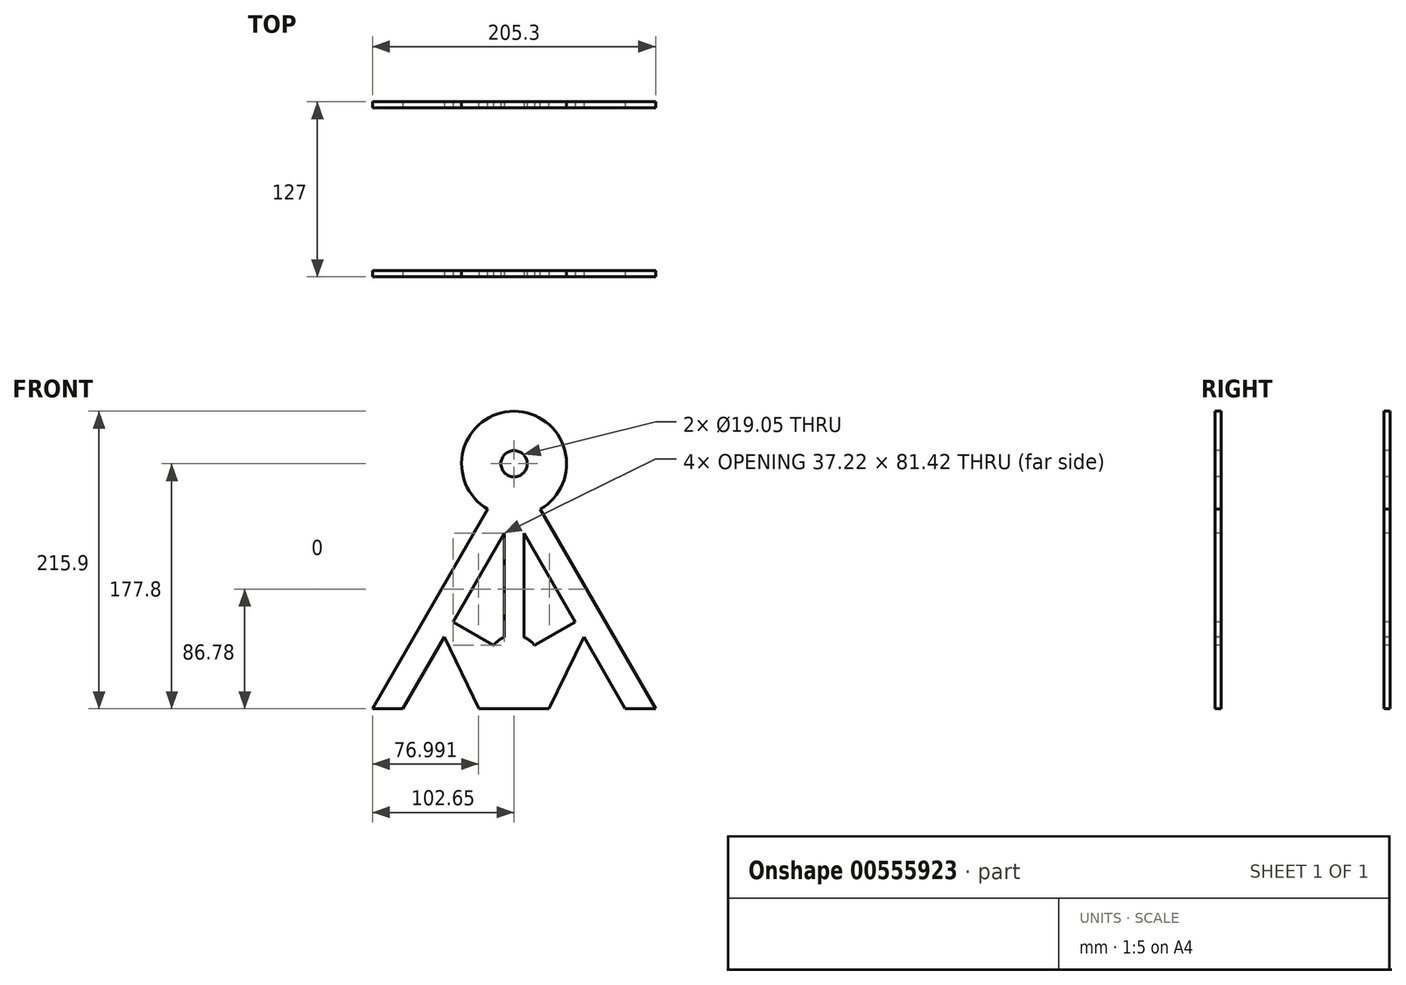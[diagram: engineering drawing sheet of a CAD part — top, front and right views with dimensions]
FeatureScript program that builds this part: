
annotation { "Feature Type Name" : "Feature", "Feature Type Description" : "" }
export const myFeature = defineFeature(function(context is Context, id is Id, definition is map)
    precondition{}
    {
        {
            var Q0;
            Q0=qCreatedBy(makeId("Front.planeOp"),FACE);
            var sketch = newSketch(context, id + "F0", { "sketchPlane" : qUnion([Q0])});
            skArc(sketch, "E0", {"start": v(-228.6, 0) * mm, "mid": v(0, -228.6) * mm, "end": v(228.6, 0) * mm});
            skLineSegment(sketch, "E1", {"start": v(-38.1, 0) * mm, "end": v(-228.6, 0) * mm});
            skLineSegment(sketch, "E2", {"start": v(38.1, 0) * mm, "end": v(228.6, 0) * mm});
            skLineSegment(sketch, "E3", {"start": v(-19.05, -33) * mm, "end": v(-114.3, -197.97) * mm});
            skLineSegment(sketch, "E4", {"start": v(19.05, -33) * mm, "end": v(114.3, -197.97) * mm});
            skArc(sketch, "E5", {"start": v(19.05, -33) * mm, "mid": v(0, 38.1) * mm, "end": v(-19.05, -33) * mm});
            skSolve(sketch);
        }
        {
            var Q0;
            {var subQ3=sQuery(id+"F0.wireOp",EDGE,"E3");Q0=makeQuery(id+"F0.imprint","IMPRINT",FACE,{"disambiguationData":[TD([[makeQuery(id+"F0.imprint","IMPRINT",EDGE,{"derivedFrom":subQ3}),1.0]])]});}
            extrude(context, id + "F1", {"entities" : qUnion([Q0]), "depth" : 127 * mm, "offsetDistance" : 25.4 * mm});
        }
        {
            var Q0;
            Q0=makeQuery(id+"F1.opExtrude","SWEPT_FACE",FACE,{"disambiguationData":[OSD([sQuery(id+"F0.wireOp",EDGE,"E5")])]});
            var Q1;
            Q1=makeQuery(id+"F1.opExtrude","SWEPT_FACE",FACE,{"disambiguationData":[OSD([sQuery(id+"F0.wireOp",EDGE,"E4")])]});
            var Q2;
            Q2=makeQuery(id+"F1.opExtrude","SWEPT_FACE",FACE,{"disambiguationData":[OSD([sQuery(id+"F0.wireOp",EDGE,"E3")])]});
            shell(context, id + "F2", {"entities" : qUnion([Q0, Q1, Q2]), "thickness" : 4.44 * mm});
        }
        {
            var Q0;
            Q0=makeQuery(id+"F1.opExtrude","CAP_FACE",FACE,{"disambiguationData":[OSD([sQuery(id+"F0.wireOp",EDGE,"E0"),sQuery(id+"F0.wireOp",EDGE,"E3"),sQuery(id+"F0.wireOp",EDGE,"E4"),sQuery(id+"F0.wireOp",EDGE,"E5")])],"isStart":false});
            var sketch = newSketch(context, id + "F3", { "sketchPlane" : qUnion([Q0])});
            skLineSegment(sketch, "E6.0", {"start": v(7.05, -50.3) * mm, "end": v(87.84, -190.25) * mm});
            skArc(sketch, "E6.1", {"start": v(-87.84, -190.25) * mm, "mid": v(-48.4, -203.88) * mm, "end": v(-7.05, -209.43) * mm});
            skCircle(sketch, "E7", {"center": v(0, 0) * mm, "radius": 9.53 * mm});
            skLineSegment(sketch, "E8", {"start": v(-7.05, -50.3) * mm, "end": v(-7.05, -125.9) * mm});
            skLineSegment(sketch, "E9", {"start": v(7.05, -50.3) * mm, "end": v(7.05, -125.9) * mm});
            skLineSegment(sketch, "E10", {"start": v(-87.84, -190.25) * mm, "end": v(-50.62, -125.78) * mm});
            skPoint(sketch, "E11.endSnap0", {"position": v(-66.67, -115.48) * mm});
            skLineSegment(sketch, "E12", {"start": v(-44.27, -114.78) * mm, "end": v(-14.9, -131.73) * mm});
            skLineSegment(sketch, "E13.trimOffspring", {"start": v(-7.05, -169.35) * mm, "end": v(-7.05, -209.43) * mm});
            skLineSegment(sketch, "E14.trimOffspring", {"start": v(-50.62, -125.78) * mm, "end": v(-87.84, -190.25) * mm});
            skArc(sketch, "E15.trimOffspring", {"start": v(7.05, -209.43) * mm, "mid": v(48.4, -203.88) * mm, "end": v(87.84, -190.25) * mm});
            skLineSegment(sketch, "E16", {"start": v(-7.05, -50.3) * mm, "end": v(0, -50.3) * mm, "construction": true});
            skLineSegment(sketch, "E17", {"start": v(0, -50.3) * mm, "end": v(0, -85.39) * mm, "construction": true});
            skLineSegment(sketch, "E18", {"start": v(-44.27, -114.78) * mm, "end": v(-7.05, -50.3) * mm});
            skLineSegment(sketch, "E19.MirrorCS", {"start": v(44.27, -114.78) * mm, "end": v(14.9, -131.73) * mm});
            skLineSegment(sketch, "E20.trimOffspring", {"start": v(7.05, -169.35) * mm, "end": v(7.05, -209.43) * mm});
            skArc(sketch, "E21", {"start": v(14.9, -131.73) * mm, "mid": v(11.36, -128.3) * mm, "end": v(7.05, -125.9) * mm});
            skPoint(sketch, "E22.orphan", {"position": v(7.05, -136.27) * mm});
            skPoint(sketch, "E23.orphan", {"position": v(7.05, -150.93) * mm});
            skPoint(sketch, "E24.orphan", {"position": v(-7.05, -150.93) * mm});
            skPoint(sketch, "E25.orphan", {"position": v(-7.05, -136.27) * mm});
            skLineSegment(sketch, "E26", {"start": v(50.62, -125.78) * mm, "end": v(7.05, -169.35) * mm, "construction": true});
            skLineSegment(sketch, "E27", {"start": v(50.62, -125.78) * mm, "end": v(7.05, -169.35) * mm});
            skLineSegment(sketch, "E28.MirrorCS", {"start": v(-50.62, -125.78) * mm, "end": v(-7.05, -169.35) * mm});
            skArc(sketch, "E29.trimOffspring", {"start": v(-7.05, -125.9) * mm, "mid": v(-11.36, -128.3) * mm, "end": v(-14.9, -131.73) * mm});
            skSolve(sketch);
        }
        {
            var Q0;
            Q0=makeQuery(id+"F3.imprint","IMPRINT",FACE,{"disambiguationData":[TD([[makeQuery(id+"F3.imprint","IMPRINT",EDGE,{"derivedFrom":sQuery(id+"F3.wireOp",EDGE,"E6.1")}),1.0]])]});
            var Q1;
            {var subQ2=sQuery(id+"F3.wireOp",EDGE,"E15.trimOffspring");Q1=makeQuery(id+"F3.imprint","IMPRINT",FACE,{"disambiguationData":[TD([[makeQuery(id+"F3.imprint","IMPRINT",EDGE,{"derivedFrom":subQ2}),1.0]])]});}
            var Q2;
            {var subQ0=sQuery(id+"F3.wireOp",EDGE,"E9");Q2=makeQuery(id+"F3.imprint","IMPRINT",FACE,{"disambiguationData":[TD([[makeQuery(id+"F3.imprint","IMPRINT",EDGE,{"derivedFrom":subQ0}),1.0]])]});}
            var Q3;
            {var subQ0=sQuery(id+"F3.wireOp",EDGE,"E8");Q3=makeQuery(id+"F3.imprint","IMPRINT",FACE,{"disambiguationData":[TD([[makeQuery(id+"F3.imprint","IMPRINT",EDGE,{"derivedFrom":subQ0}),-1.0]])]});}
            var Q4;
            Q4=makeQuery(id+"F3.imprint","IMPRINT",FACE,{"disambiguationData":[TD([[makeQuery(id+"F3.imprint","IMPRINT",EDGE,{"derivedFrom":sQuery(id+"F3.wireOp",EDGE,"E7")}),1.0]])]});
            var Q5;
            Q5=makeQuery(id+"F1.opExtrude","CAP_FACE",FACE,{"disambiguationData":[OSD([sQuery(id+"F0.wireOp",EDGE,"E0"),sQuery(id+"F0.wireOp",EDGE,"E3"),sQuery(id+"F0.wireOp",EDGE,"E4"),sQuery(id+"F0.wireOp",EDGE,"E5")])],"isStart":true});
            extrude(context, id + "F4", {"entities" : qUnion([Q0, Q1, Q2, Q3, Q4]), "operationType" : NewBodyOperationType.REMOVE, "endBound" : BoundingType.UP_TO_SURFACE, "oppositeDirection" : true, "depth" : 25.4 * mm, "endBoundEntityFace" : qUnion([Q5]), "offsetDistance" : 25.4 * mm});
        }
        {
            var Q0;
            Q0=qCreatedBy(makeId("Front.planeOp"),FACE);
            var sketch = newSketch(context, id + "F5", { "sketchPlane" : qUnion([Q0])});
            skLineSegment(sketch, "E30", {"start": v(0, -228.6) * mm, "end": v(114.3, -228.6) * mm});
            skLineSegment(sketch, "E31", {"start": v(0, -228.6) * mm, "end": v(-114.3, -228.6) * mm});
            skLineSegment(sketch, "E32", {"start": v(114.3, -197.97) * mm, "end": v(114.3, -228.6) * mm});
            skLineSegment(sketch, "E33", {"start": v(-114.3, -197.97) * mm, "end": v(-114.3, -228.6) * mm});
            skPoint(sketch, "E34.orphan", {"position": v(-122.47, -228.6) * mm});
            skArc(sketch, "E35.0", {"start": v(-114.3, -197.97) * mm, "mid": v(0, -228.6) * mm, "end": v(114.3, -197.97) * mm});
            skLineSegment(sketch, "E36", {"start": v(114.3, -228.6) * mm, "end": v(107.95, -228.6) * mm, "construction": true});
            skLineSegment(sketch, "E37", {"start": v(107.95, -228.6) * mm, "end": v(107.95, -222.25) * mm, "construction": true});
            skLineSegment(sketch, "E38.bottom", {"start": v(107.95, -222.25) * mm, "end": v(101.6, -222.25) * mm});
            skLineSegment(sketch, "E38.left", {"start": v(107.95, -222.25) * mm, "end": v(107.95, -215.9) * mm});
            skLineSegment(sketch, "E38.right", {"start": v(88.9, -222.25) * mm, "end": v(88.9, -215.9) * mm});
            skLineSegment(sketch, "E39", {"start": v(101.6, -222.25) * mm, "end": v(101.6, -215.9) * mm});
            skLineSegment(sketch, "E40", {"start": v(95.25, -222.25) * mm, "end": v(95.25, -215.9) * mm});
            skLineSegment(sketch, "E41.trimOffspring", {"start": v(95.25, -222.25) * mm, "end": v(88.9, -222.25) * mm});
            skLineSegment(sketch, "E42", {"start": v(104.78, -215.9) * mm, "end": v(104.78, -212.72) * mm, "construction": true});
            skLineSegment(sketch, "E43", {"start": v(92.08, -215.9) * mm, "end": v(92.08, -212.72) * mm, "construction": true});
            skLineSegment(sketch, "E44", {"start": v(107.95, -215.9) * mm, "end": v(104.78, -212.72) * mm});
            skLineSegment(sketch, "E45", {"start": v(101.6, -215.9) * mm, "end": v(104.78, -212.72) * mm});
            skLineSegment(sketch, "E46", {"start": v(95.25, -215.9) * mm, "end": v(92.08, -212.72) * mm});
            skLineSegment(sketch, "E47", {"start": v(88.9, -215.9) * mm, "end": v(92.08, -212.72) * mm});
            skLineSegment(sketch, "E48.MirrorCS", {"start": v(-104.78, -215.9) * mm, "end": v(-104.78, -212.72) * mm, "construction": true});
            skLineSegment(sketch, "E49.MirrorCS", {"start": v(-92.08, -215.9) * mm, "end": v(-92.08, -212.72) * mm, "construction": true});
            skLineSegment(sketch, "E50.MirrorCS", {"start": v(-101.6, -215.9) * mm, "end": v(-104.78, -212.72) * mm});
            skLineSegment(sketch, "E51.MirrorCS", {"start": v(-88.9, -215.9) * mm, "end": v(-92.08, -212.72) * mm});
            skLineSegment(sketch, "E52.MirrorCS", {"start": v(-107.95, -215.9) * mm, "end": v(-104.78, -212.72) * mm});
            skLineSegment(sketch, "E53.MirrorCS", {"start": v(-95.25, -222.25) * mm, "end": v(-95.25, -215.9) * mm});
            skLineSegment(sketch, "E54.MirrorCS", {"start": v(-101.6, -222.25) * mm, "end": v(-101.6, -215.9) * mm});
            skLineSegment(sketch, "E55.MirrorCS", {"start": v(-107.95, -222.25) * mm, "end": v(-107.95, -215.9) * mm});
            skLineSegment(sketch, "E56.MirrorCS", {"start": v(-107.95, -222.25) * mm, "end": v(-101.6, -222.25) * mm});
            skLineSegment(sketch, "E57.MirrorCS", {"start": v(-88.9, -222.25) * mm, "end": v(-88.9, -215.9) * mm});
            skLineSegment(sketch, "E58.MirrorCS", {"start": v(-95.25, -215.9) * mm, "end": v(-92.08, -212.72) * mm});
            skLineSegment(sketch, "E59.MirrorCS", {"start": v(-95.25, -222.25) * mm, "end": v(-88.9, -222.25) * mm});
            skSolve(sketch);
        }
        {
            var Q0;
            {var subQ2=sQuery(id+"F5.wireOp",EDGE,"E30");Q0=makeQuery(id+"F5.imprint","IMPRINT",FACE,{"disambiguationData":[TD([[makeQuery(id+"F5.imprint","IMPRINT",EDGE,{"derivedFrom":subQ2}),1.0]])]});}
            var Q1;
            {var subQ2=sQuery(id+"F5.wireOp",EDGE,"E31");Q1=makeQuery(id+"F5.imprint","IMPRINT",FACE,{"disambiguationData":[TD([[makeQuery(id+"F5.imprint","IMPRINT",EDGE,{"derivedFrom":subQ2}),-1.0]])]});}
            var Q2;
            Q2=makeQuery(id+"F1.opExtrude","CAP_FACE",FACE,{"disambiguationData":[OSD([sQuery(id+"F0.wireOp",EDGE,"E0"),sQuery(id+"F0.wireOp",EDGE,"E3"),sQuery(id+"F0.wireOp",EDGE,"E4"),sQuery(id+"F0.wireOp",EDGE,"E5")])],"isStart":false});
            extrude(context, id + "F6", {"entities" : qUnion([Q0, Q1]), "operationType" : NewBodyOperationType.ADD, "endBound" : BoundingType.UP_TO_SURFACE, "depth" : 25.4 * mm, "endBoundEntityFace" : qUnion([Q2]), "offsetDistance" : 25.4 * mm});
        }
        {
            var Q0;
            {var subQ0=sQuery(id+"F5.wireOp",EDGE,"E35.0");Q0=makeQuery(id+"F6.boolean.opBoolean","MERGE",FACE,{"derivedFrom":[makeQuery(id+"F1.opExtrude","CAP_FACE",FACE,{"disambiguationData":[OSD([sQuery(id+"F0.wireOp",EDGE,"E0"),sQuery(id+"F0.wireOp",EDGE,"E3"),sQuery(id+"F0.wireOp",EDGE,"E4"),sQuery(id+"F0.wireOp",EDGE,"E5")])],"isStart":false}),makeQuery(id+"F6.opExtrude","CAP_FACE",FACE,{"disambiguationData":[OSD([sQuery(id+"F5.wireOp",EDGE,"E30"),sQuery(id+"F5.wireOp",EDGE,"E32"),subQ0,sQuery(id+"F5.wireOp",EDGE,"E38.bottom"),sQuery(id+"F5.wireOp",EDGE,"E38.left"),sQuery(id+"F5.wireOp",EDGE,"E38.right"),sQuery(id+"F5.wireOp",EDGE,"E39"),sQuery(id+"F5.wireOp",EDGE,"E40"),sQuery(id+"F5.wireOp",EDGE,"E41.trimOffspring"),sQuery(id+"F5.wireOp",EDGE,"E44"),sQuery(id+"F5.wireOp",EDGE,"E45"),sQuery(id+"F5.wireOp",EDGE,"E46"),sQuery(id+"F5.wireOp",EDGE,"E47")])],"isStart":false}),makeQuery(id+"F6.opExtrude","CAP_FACE",FACE,{"disambiguationData":[OSD([sQuery(id+"F5.wireOp",EDGE,"E31"),sQuery(id+"F5.wireOp",EDGE,"E33"),subQ0,sQuery(id+"F5.wireOp",EDGE,"E50.MirrorCS"),sQuery(id+"F5.wireOp",EDGE,"E51.MirrorCS"),sQuery(id+"F5.wireOp",EDGE,"E52.MirrorCS"),sQuery(id+"F5.wireOp",EDGE,"E53.MirrorCS"),sQuery(id+"F5.wireOp",EDGE,"E54.MirrorCS"),sQuery(id+"F5.wireOp",EDGE,"E55.MirrorCS"),sQuery(id+"F5.wireOp",EDGE,"E56.MirrorCS"),sQuery(id+"F5.wireOp",EDGE,"E57.MirrorCS"),sQuery(id+"F5.wireOp",EDGE,"E58.MirrorCS"),sQuery(id+"F5.wireOp",EDGE,"E59.MirrorCS")])],"isStart":false})]});}
            var sketch = newSketch(context, id + "F7", { "sketchPlane" : qUnion([Q0])});
            skLineSegment(sketch, "E60", {"start": v(0, 0) * mm, "end": v(0, -177.8) * mm, "construction": true});
            skLineSegment(sketch, "E61", {"start": v(0, -177.8) * mm, "end": v(-132.58, -177.8) * mm});
            skLineSegment(sketch, "E62.bottom", {"start": v(-132.58, -177.8) * mm, "end": v(117.74, -177.8) * mm});
            skLineSegment(sketch, "E62.top", {"start": v(-132.58, 43.64) * mm, "end": v(117.74, 43.64) * mm});
            skLineSegment(sketch, "E62.left", {"start": v(-132.58, -177.8) * mm, "end": v(-132.58, 43.64) * mm});
            skLineSegment(sketch, "E62.right", {"start": v(117.74, -177.8) * mm, "end": v(117.74, 43.64) * mm});
            skSolve(sketch);
        }
        {
            var Q0;
            {var subQ1=makeQuery(id+"F1.opExtrude","CAP_EDGE",EDGE,{"disambiguationData":[OSD([sQuery(id+"F0.wireOp",EDGE,"E5")])],"isStart":false});Q0=makeQuery(id+"F7.imprint","IMPRINT",FACE,{"disambiguationData":[TD([[makeQuery(id+"F7.imprint","IMPRINT",EDGE,{"derivedFrom":subQ1}),1.0]])]});}
            var Q1;
            {var subQ0=sQuery(id+"F5.wireOp",EDGE,"E35.0");Q1=makeQuery(id+"F6.boolean.opBoolean","MERGE",FACE,{"derivedFrom":[makeQuery(id+"F1.opExtrude","CAP_FACE",FACE,{"disambiguationData":[OSD([sQuery(id+"F0.wireOp",EDGE,"E0"),sQuery(id+"F0.wireOp",EDGE,"E3"),sQuery(id+"F0.wireOp",EDGE,"E4"),sQuery(id+"F0.wireOp",EDGE,"E5")])],"isStart":true}),makeQuery(id+"F6.opExtrude","CAP_FACE",FACE,{"disambiguationData":[OSD([sQuery(id+"F5.wireOp",EDGE,"E30"),sQuery(id+"F5.wireOp",EDGE,"E32"),subQ0,sQuery(id+"F5.wireOp",EDGE,"E38.bottom"),sQuery(id+"F5.wireOp",EDGE,"E38.left"),sQuery(id+"F5.wireOp",EDGE,"E38.right"),sQuery(id+"F5.wireOp",EDGE,"E39"),sQuery(id+"F5.wireOp",EDGE,"E40"),sQuery(id+"F5.wireOp",EDGE,"E41.trimOffspring"),sQuery(id+"F5.wireOp",EDGE,"E44"),sQuery(id+"F5.wireOp",EDGE,"E45"),sQuery(id+"F5.wireOp",EDGE,"E46"),sQuery(id+"F5.wireOp",EDGE,"E47")])],"isStart":true}),makeQuery(id+"F6.opExtrude","CAP_FACE",FACE,{"disambiguationData":[OSD([sQuery(id+"F5.wireOp",EDGE,"E31"),sQuery(id+"F5.wireOp",EDGE,"E33"),subQ0,sQuery(id+"F5.wireOp",EDGE,"E50.MirrorCS"),sQuery(id+"F5.wireOp",EDGE,"E51.MirrorCS"),sQuery(id+"F5.wireOp",EDGE,"E52.MirrorCS"),sQuery(id+"F5.wireOp",EDGE,"E53.MirrorCS"),sQuery(id+"F5.wireOp",EDGE,"E54.MirrorCS"),sQuery(id+"F5.wireOp",EDGE,"E55.MirrorCS"),sQuery(id+"F5.wireOp",EDGE,"E56.MirrorCS"),sQuery(id+"F5.wireOp",EDGE,"E57.MirrorCS"),sQuery(id+"F5.wireOp",EDGE,"E58.MirrorCS"),sQuery(id+"F5.wireOp",EDGE,"E59.MirrorCS")])],"isStart":true})]});}
            extrude(context, id + "F8", {"entities" : qUnion([Q0]), "operationType" : NewBodyOperationType.INTERSECT, "endBound" : BoundingType.UP_TO_SURFACE, "oppositeDirection" : true, "depth" : 218.44 * mm, "endBoundEntityFace" : qUnion([Q1]), "offsetDistance" : 25.4 * mm});
        }
        {
            var Q0;
            {var subQ0=sQuery(id+"F5.wireOp",EDGE,"E35.0");Q0=makeQuery(id+"F6.boolean.opBoolean","MERGE",FACE,{"derivedFrom":[makeQuery(id+"F1.opExtrude","CAP_FACE",FACE,{"disambiguationData":[OSD([sQuery(id+"F0.wireOp",EDGE,"E0"),sQuery(id+"F0.wireOp",EDGE,"E3"),sQuery(id+"F0.wireOp",EDGE,"E4"),sQuery(id+"F0.wireOp",EDGE,"E5")])],"isStart":false}),makeQuery(id+"F6.opExtrude","CAP_FACE",FACE,{"disambiguationData":[OSD([sQuery(id+"F5.wireOp",EDGE,"E30"),sQuery(id+"F5.wireOp",EDGE,"E32"),subQ0,sQuery(id+"F5.wireOp",EDGE,"E38.bottom"),sQuery(id+"F5.wireOp",EDGE,"E38.left"),sQuery(id+"F5.wireOp",EDGE,"E38.right"),sQuery(id+"F5.wireOp",EDGE,"E39"),sQuery(id+"F5.wireOp",EDGE,"E40"),sQuery(id+"F5.wireOp",EDGE,"E41.trimOffspring"),sQuery(id+"F5.wireOp",EDGE,"E44"),sQuery(id+"F5.wireOp",EDGE,"E45"),sQuery(id+"F5.wireOp",EDGE,"E46"),sQuery(id+"F5.wireOp",EDGE,"E47")])],"isStart":false}),makeQuery(id+"F6.opExtrude","CAP_FACE",FACE,{"disambiguationData":[OSD([sQuery(id+"F5.wireOp",EDGE,"E31"),sQuery(id+"F5.wireOp",EDGE,"E33"),subQ0,sQuery(id+"F5.wireOp",EDGE,"E50.MirrorCS"),sQuery(id+"F5.wireOp",EDGE,"E51.MirrorCS"),sQuery(id+"F5.wireOp",EDGE,"E52.MirrorCS"),sQuery(id+"F5.wireOp",EDGE,"E53.MirrorCS"),sQuery(id+"F5.wireOp",EDGE,"E54.MirrorCS"),sQuery(id+"F5.wireOp",EDGE,"E55.MirrorCS"),sQuery(id+"F5.wireOp",EDGE,"E56.MirrorCS"),sQuery(id+"F5.wireOp",EDGE,"E57.MirrorCS"),sQuery(id+"F5.wireOp",EDGE,"E58.MirrorCS"),sQuery(id+"F5.wireOp",EDGE,"E59.MirrorCS")])],"isStart":false})]});}
            var sketch = newSketch(context, id + "F9", { "sketchPlane" : qUnion([Q0])});
            skLineSegment(sketch, "E63", {"start": v(0, -177.8) * mm, "end": v(-25.4, -177.8) * mm});
            skLineSegment(sketch, "E64", {"start": v(0, -177.8) * mm, "end": v(25.4, -177.8) * mm});
            skLineSegment(sketch, "E65", {"start": v(-25.4, -177.8) * mm, "end": v(-50.62, -125.78) * mm});
            skLineSegment(sketch, "E66", {"start": v(25.4, -177.8) * mm, "end": v(50.62, -125.78) * mm});
            skLineSegment(sketch, "E67.0", {"start": v(-50.62, -125.78) * mm, "end": v(-7.05, -169.35) * mm});
            skLineSegment(sketch, "E68.0", {"start": v(-7.05, -169.35) * mm, "end": v(-7.05, -177.8) * mm});
            skLineSegment(sketch, "E69.0", {"start": v(7.05, -169.35) * mm, "end": v(7.05, -177.8) * mm});
            skLineSegment(sketch, "E70.0", {"start": v(50.62, -125.78) * mm, "end": v(7.05, -169.35) * mm});
            skSolve(sketch);
        }
        {
            var Q0;
            {var subQ2=sQuery(id+"F9.wireOp",EDGE,"E65");Q0=makeQuery(id+"F9.imprint","IMPRINT",FACE,{"disambiguationData":[TD([[makeQuery(id+"F9.imprint","IMPRINT",EDGE,{"derivedFrom":subQ2}),-1.0]])]});}
            var Q1;
            {var subQ2=sQuery(id+"F9.wireOp",EDGE,"E66");Q1=makeQuery(id+"F9.imprint","IMPRINT",FACE,{"disambiguationData":[TD([[makeQuery(id+"F9.imprint","IMPRINT",EDGE,{"derivedFrom":subQ2}),1.0]])]});}
            var Q2;
            {var subQ0=sQuery(id+"F0.wireOp",EDGE,"E5");var subQ1=sQuery(id+"F0.wireOp",EDGE,"E4");var subQ2=sQuery(id+"F0.wireOp",EDGE,"E3");var subQ3=sQuery(id+"F0.wireOp",EDGE,"E0");Q2=makeQuery(id+"F2.opShell","OFFSET_FACE",FACE,{"disambiguationData":[OSD([subQ3,subQ2,subQ1,subQ0]),TDD([makeQuery(id+"F1.opExtrude","CAP_FACE",FACE,{"disambiguationData":[OSD([subQ3,subQ2,subQ1,subQ0])],"isStart":false})])]});}
            extrude(context, id + "F10", {"entities" : qUnion([Q0, Q1]), "operationType" : NewBodyOperationType.ADD, "endBound" : BoundingType.UP_TO_SURFACE, "oppositeDirection" : true, "depth" : 25.4 * mm, "endBoundEntityFace" : qUnion([Q2]), "offsetDistance" : 25.4 * mm});
        }
        {
            var Q0;
            {var subQ0=sQuery(id+"F5.wireOp",EDGE,"E35.0");Q0=makeQuery(id+"F6.boolean.opBoolean","MERGE",FACE,{"derivedFrom":[makeQuery(id+"F1.opExtrude","CAP_FACE",FACE,{"disambiguationData":[OSD([sQuery(id+"F0.wireOp",EDGE,"E0"),sQuery(id+"F0.wireOp",EDGE,"E3"),sQuery(id+"F0.wireOp",EDGE,"E4"),sQuery(id+"F0.wireOp",EDGE,"E5")])],"isStart":true}),makeQuery(id+"F6.opExtrude","CAP_FACE",FACE,{"disambiguationData":[OSD([sQuery(id+"F5.wireOp",EDGE,"E30"),sQuery(id+"F5.wireOp",EDGE,"E32"),subQ0,sQuery(id+"F5.wireOp",EDGE,"E38.bottom"),sQuery(id+"F5.wireOp",EDGE,"E38.left"),sQuery(id+"F5.wireOp",EDGE,"E38.right"),sQuery(id+"F5.wireOp",EDGE,"E39"),sQuery(id+"F5.wireOp",EDGE,"E40"),sQuery(id+"F5.wireOp",EDGE,"E41.trimOffspring"),sQuery(id+"F5.wireOp",EDGE,"E44"),sQuery(id+"F5.wireOp",EDGE,"E45"),sQuery(id+"F5.wireOp",EDGE,"E46"),sQuery(id+"F5.wireOp",EDGE,"E47")])],"isStart":true}),makeQuery(id+"F6.opExtrude","CAP_FACE",FACE,{"disambiguationData":[OSD([sQuery(id+"F5.wireOp",EDGE,"E31"),sQuery(id+"F5.wireOp",EDGE,"E33"),subQ0,sQuery(id+"F5.wireOp",EDGE,"E50.MirrorCS"),sQuery(id+"F5.wireOp",EDGE,"E51.MirrorCS"),sQuery(id+"F5.wireOp",EDGE,"E52.MirrorCS"),sQuery(id+"F5.wireOp",EDGE,"E53.MirrorCS"),sQuery(id+"F5.wireOp",EDGE,"E54.MirrorCS"),sQuery(id+"F5.wireOp",EDGE,"E55.MirrorCS"),sQuery(id+"F5.wireOp",EDGE,"E56.MirrorCS"),sQuery(id+"F5.wireOp",EDGE,"E57.MirrorCS"),sQuery(id+"F5.wireOp",EDGE,"E58.MirrorCS"),sQuery(id+"F5.wireOp",EDGE,"E59.MirrorCS")])],"isStart":true})]});}
            var sketch = newSketch(context, id + "F11", { "sketchPlane" : qUnion([Q0])});
            skLineSegment(sketch, "E71", {"start": v(0, -177.8) * mm, "end": v(-25.4, -177.8) * mm});
            skLineSegment(sketch, "E72", {"start": v(0, -177.8) * mm, "end": v(25.4, -177.8) * mm});
            skLineSegment(sketch, "E73.0", {"start": v(-7.05, -177.8) * mm, "end": v(-7.05, -169.35) * mm});
            skLineSegment(sketch, "E74.0", {"start": v(7.05, -177.8) * mm, "end": v(7.05, -169.35) * mm});
            skLineSegment(sketch, "E75.0", {"start": v(-7.05, -169.35) * mm, "end": v(-50.62, -125.78) * mm});
            skLineSegment(sketch, "E76.0", {"start": v(7.05, -169.35) * mm, "end": v(50.62, -125.78) * mm});
            skLineSegment(sketch, "E77", {"start": v(-25.4, -177.8) * mm, "end": v(-50.62, -125.78) * mm});
            skLineSegment(sketch, "E78", {"start": v(25.4, -177.8) * mm, "end": v(50.62, -125.78) * mm});
            skSolve(sketch);
        }
        {
            var Q0;
            {var subQ0=sQuery(id+"F11.wireOp",EDGE,"E74.0");Q0=makeQuery(id+"F11.imprint","IMPRINT",FACE,{"disambiguationData":[TD([[makeQuery(id+"F11.imprint","IMPRINT",EDGE,{"derivedFrom":subQ0}),-1.0]])]});}
            var Q1;
            {var subQ0=sQuery(id+"F11.wireOp",EDGE,"E73.0");Q1=makeQuery(id+"F11.imprint","IMPRINT",FACE,{"disambiguationData":[TD([[makeQuery(id+"F11.imprint","IMPRINT",EDGE,{"derivedFrom":subQ0}),1.0]])]});}
            var Q2;
            {var subQ0=sQuery(id+"F0.wireOp",EDGE,"E5");var subQ1=sQuery(id+"F0.wireOp",EDGE,"E4");var subQ2=sQuery(id+"F0.wireOp",EDGE,"E3");var subQ3=sQuery(id+"F0.wireOp",EDGE,"E0");Q2=makeQuery(id+"F2.opShell","OFFSET_FACE",FACE,{"disambiguationData":[OSD([subQ3,subQ2,subQ1,subQ0]),TDD([makeQuery(id+"F1.opExtrude","CAP_FACE",FACE,{"disambiguationData":[OSD([subQ3,subQ2,subQ1,subQ0])],"isStart":true})])]});}
            extrude(context, id + "F12", {"entities" : qUnion([Q0, Q1]), "operationType" : NewBodyOperationType.ADD, "endBound" : BoundingType.UP_TO_SURFACE, "oppositeDirection" : true, "depth" : 25.4 * mm, "endBoundEntityFace" : qUnion([Q2]), "offsetDistance" : 25.4 * mm});
        }
    });
